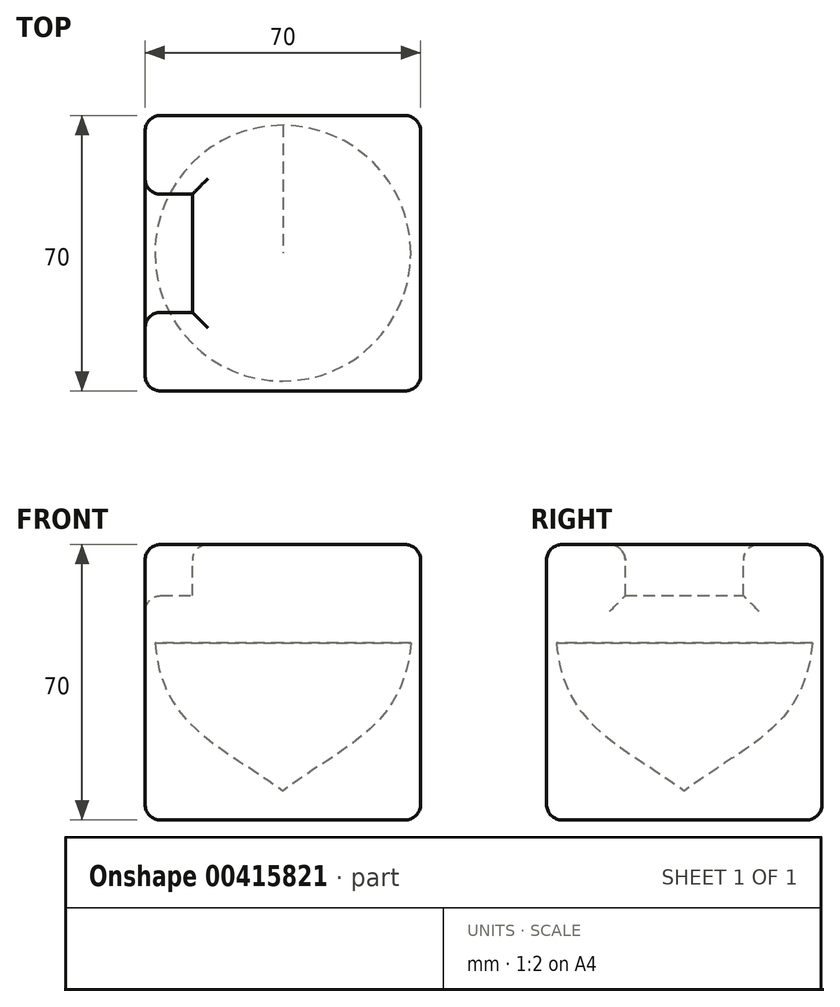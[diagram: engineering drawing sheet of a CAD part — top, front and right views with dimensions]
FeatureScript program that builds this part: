
annotation { "Feature Type Name" : "Feature", "Feature Type Description" : "" }
export const myFeature = defineFeature(function(context is Context, id is Id, definition is map)
    precondition{}
    {
        {
            var Q0;
            Q0=qCreatedBy(makeId("Top.planeOp"),FACE);
            var sketch = newSketch(context, id + "F0", { "sketchPlane" : qUnion([Q0])});
            skLineSegment(sketch, "E0.bottom", {"start": v(35, -35) * mm, "end": v(-35, -35) * mm});
            skLineSegment(sketch, "E0.top", {"start": v(35, 35) * mm, "end": v(-35, 35) * mm});
            skLineSegment(sketch, "E0.left", {"start": v(35, -35) * mm, "end": v(35, 35) * mm});
            skLineSegment(sketch, "E0.right", {"start": v(-35, -35) * mm, "end": v(-35, 35) * mm});
            skPoint(sketch, "E0.middle", {"position": v(0, 0) * mm});
            skSolve(sketch);
        }
        {
            var Q0;
            Q0 = qSketchRegion(id + "F0", true);
            extrude(context, id + "F1", {"entities" : qUnion([Q0]), "endBound" : BoundingType.SYMMETRIC, "depth" : 70 * mm});
        }
        {
            var Q0;
            Q0=makeQuery(id+"F1.opExtrude","CAP_FACE",FACE,{"disambiguationData":[OSD([sQuery(id+"F0.wireOp",EDGE,"E0.bottom"),sQuery(id+"F0.wireOp",EDGE,"E0.top"),sQuery(id+"F0.wireOp",EDGE,"E0.left"),sQuery(id+"F0.wireOp",EDGE,"E0.right")])],"isStart":false});
            var sketch = newSketch(context, id + "F2", { "sketchPlane" : qUnion([Q0])});
            skLineSegment(sketch, "E1.bottom", {"start": v(-35, -15) * mm, "end": v(-23, -15) * mm});
            skLineSegment(sketch, "E1.top", {"start": v(-35, 15) * mm, "end": v(-23, 15) * mm});
            skLineSegment(sketch, "E1.left", {"start": v(-35, -15) * mm, "end": v(-35, 15) * mm});
            skLineSegment(sketch, "E1.right", {"start": v(-23, -15) * mm, "end": v(-23, 15) * mm});
            skPoint(sketch, "E1.middle", {"position": v(-29, 0) * mm});
            skPoint(sketch, "E1.middle.positionSnap0", {"position": v(-35, 0) * mm});
            skPoint(sketch, "E1.centerSnap0", {"position": v(-35, 0) * mm});
            skSolve(sketch);
        }
        {
            var Q0;
            Q0 = qSketchRegion(id + "F2", true);
            extrude(context, id + "F3", {"entities" : qUnion([Q0]), "operationType" : NewBodyOperationType.REMOVE, "oppositeDirection" : true, "depth" : 13 * mm});
        }
        {
            var Q0;
            Q0=makeQuery(id+"F1.opExtrude","SWEPT_FACE",FACE,{"disambiguationData":[OSD([sQuery(id+"F0.wireOp",EDGE,"E0.bottom")])]});
            var Q1;
            Q1=makeQuery(id+"F1.opExtrude","SWEPT_FACE",FACE,{"disambiguationData":[OSD([sQuery(id+"F0.wireOp",EDGE,"E0.left")])]});
            var Q2;
            Q2=makeQuery(id+"F1.opExtrude","SWEPT_FACE",FACE,{"disambiguationData":[OSD([sQuery(id+"F0.wireOp",EDGE,"E0.top")])]});
            var Q3;
            Q3=makeQuery(id+"F1.opExtrude","SWEPT_FACE",FACE,{"disambiguationData":[OSD([sQuery(id+"F0.wireOp",EDGE,"E0.right")])]});
            var Q4;
            Q4=makeQuery(id+"F1.opExtrude","CAP_FACE",FACE,{"disambiguationData":[OSD([sQuery(id+"F0.wireOp",EDGE,"E0.bottom"),sQuery(id+"F0.wireOp",EDGE,"E0.top"),sQuery(id+"F0.wireOp",EDGE,"E0.left"),sQuery(id+"F0.wireOp",EDGE,"E0.right")])],"isStart":false});
            fillet(context, id + "F4", {"entities" : qUnion([Q0, Q1, Q2, Q3, Q4]), "radius" : 4 * mm, "tangentPropagation" : true, "allowEdgeOverflow" : false});
        }
        {
            var Q0;
            Q0=qCreatedBy(makeId("Top.planeOp"),FACE);
            var sketch = newSketch(context, id + "F5", { "sketchPlane" : qUnion([Q0])});
            skLineSegment(sketch, "E2", {"start": v(0, 0) * mm, "end": v(0, 35) * mm, "construction": true});
            skLineSegment(sketch, "E3", {"start": v(0.5, 35) * mm, "end": v(0.5, 0) * mm});
            skLineSegment(sketch, "E4", {"start": v(0.5, 0) * mm, "end": v(-0.5, 0) * mm});
            skLineSegment(sketch, "E5", {"start": v(-0.5, 0) * mm, "end": v(-0.5, 35) * mm});
            skLineSegment(sketch, "E6", {"start": v(-0.5, 35) * mm, "end": v(0.5, 35) * mm});
            skSolve(sketch);
        }
        {
            var Q0;
            Q0 = qSketchRegion(id + "F5", true);
            extrude(context, id + "F6", {"entities" : qUnion([Q0]), "operationType" : NewBodyOperationType.ADD, "endBound" : BoundingType.UP_TO_NEXT, "oppositeDirection" : true, "depth" : 25 * mm, "hasSecondDirection" : true, "secondDirectionOppositeDirection" : false, "secondDirectionDepth" : 10 * mm});
        }
        {
            var Q0;
            Q0=qCreatedBy(makeId("Right.planeOp"),FACE);
            var sketch = newSketch(context, id + "F7", { "sketchPlane" : qUnion([Q0])});
            skLineSegment(sketch, "E7", {"start": v(0, -59.1) * mm, "end": v(0, 58.79) * mm, "construction": true});
            skSolve(sketch);
        }
        {
            var Q0;
            Q0=qCreatedBy(makeId("Right.planeOp"),FACE);
            var sketch = newSketch(context, id + "F8", { "sketchPlane" : qUnion([Q0])});
            skLineSegment(sketch, "E8", {"start": v(0, 10) * mm, "end": v(0, -27.62) * mm});
            skLineSegment(sketch, "E9", {"start": v(0, 10) * mm, "end": v(32.5, 10) * mm});
            skFitSpline(sketch, "E10", {"points": [v(32.5, 10) * mm, v(0, -27.62) * mm], "startDerivative": vector(-5.46, -64.63) * mm, "endDerivative": vector(-47.84, -35.92) * mm});
            skSolve(sketch);
        }
        {
            var Q0;
            Q0=qCreatedBy(makeId("Top.planeOp"),FACE);
            var sketch = newSketch(context, id + "F9", { "sketchPlane" : qUnion([Q0])});
            skLineSegment(sketch, "E11", {"start": v(0, 0) * mm, "end": v(-32, 32) * mm, "construction": true});
            skLineSegment(sketch, "E12", {"start": v(-0.35, -0.35) * mm, "end": v(0.35, 0.35) * mm});
            skLineSegment(sketch, "E13", {"start": v(0.35, 0.35) * mm, "end": v(-31.65, 32.35) * mm});
            skLineSegment(sketch, "E14", {"start": v(-0.35, -0.35) * mm, "end": v(-32.35, 31.65) * mm});
            skLineSegment(sketch, "E15", {"start": v(-32.35, 31.65) * mm, "end": v(-31.65, 32.35) * mm, "construction": true});
            skArc(sketch, "E16.0", {"start": v(-31, 32.5) * mm, "mid": v(-32.06, 32.06) * mm, "end": v(-32.5, 31) * mm});
            skSolve(sketch);
        }
        {
            var Q0;
            Q0 = qSketchRegion(id + "F9", true);
            extrude(context, id + "F10", {"entities" : qUnion([Q0]), "operationType" : NewBodyOperationType.ADD, "endBound" : BoundingType.UP_TO_NEXT, "oppositeDirection" : true, "depth" : 25 * mm, "hasSecondDirection" : true, "secondDirectionOppositeDirection" : false, "secondDirectionDepth" : 10 * mm});
        }
        {
            var Q0;
            Q0 = qSketchRegion(id + "F8", true);
            var Q1;
            Q1=sQuery(id+"F7.wireOp",EDGE,"E7");
            revolve(context, id + "F11", {"operationType" : NewBodyOperationType.REMOVE, "entities" : qUnion([Q0]), "axis" : qUnion([Q1]), "revolveType" : RevolveType.FULL, "oppositeDirection" : true});
        }
    });
